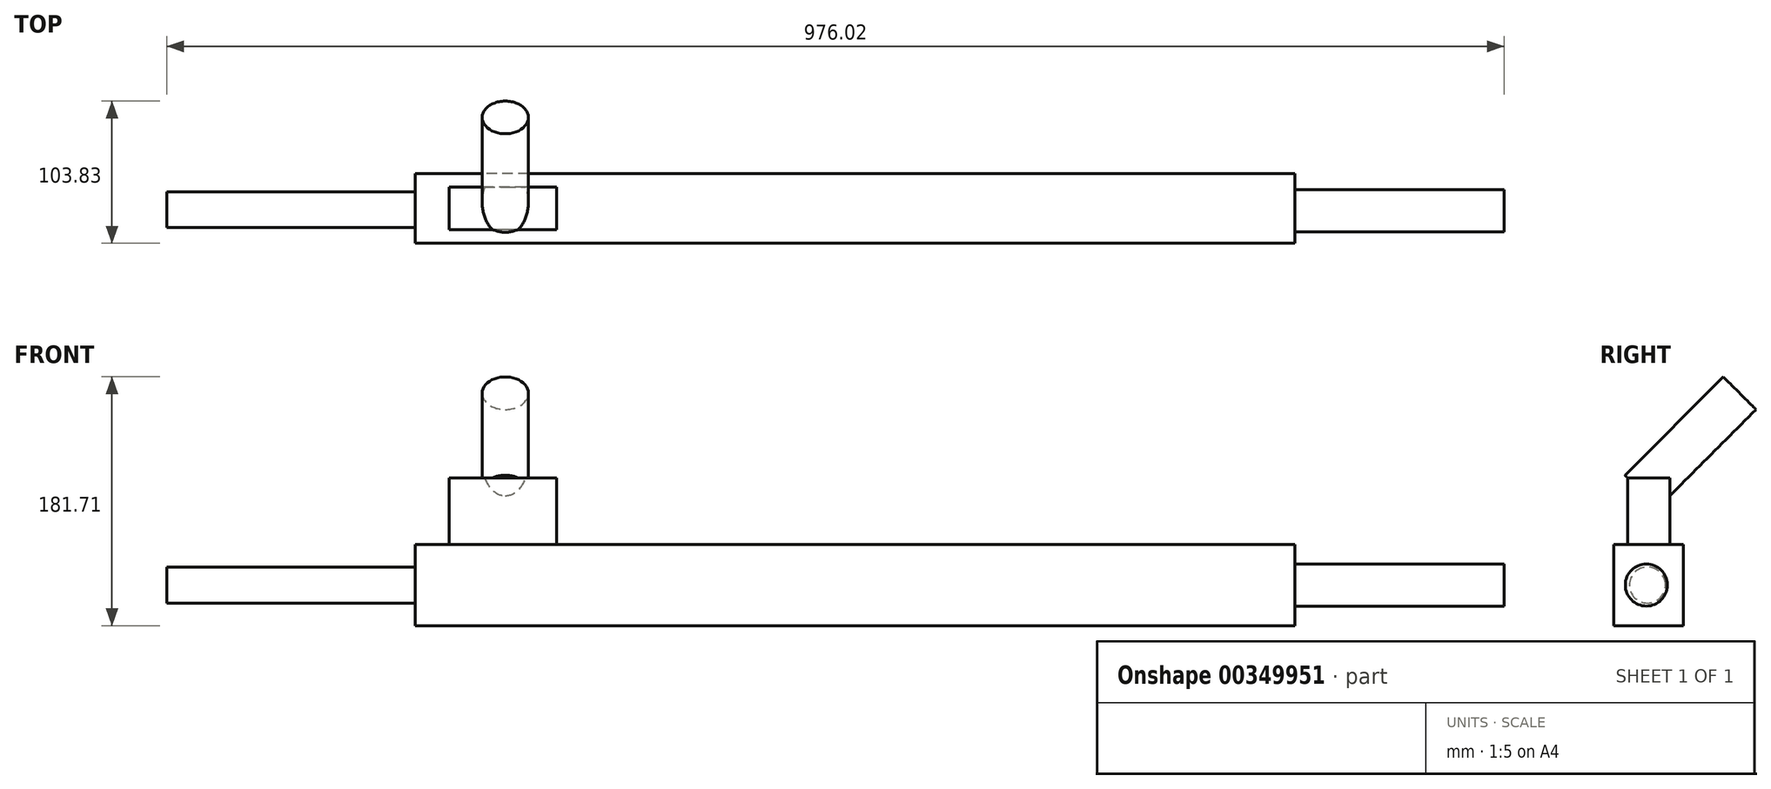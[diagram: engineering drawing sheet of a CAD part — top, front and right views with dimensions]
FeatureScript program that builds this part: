
annotation { "Feature Type Name" : "Feature", "Feature Type Description" : "" }
export const myFeature = defineFeature(function(context is Context, id is Id, definition is map)
    precondition{}
    {
        {
            var Q0;
            Q0=qCreatedBy(makeId("Front.planeOp"),FACE);
            var sketch = newSketch(context, id + "F0", { "sketchPlane" : qUnion([Q0])});
            skLineSegment(sketch, "E0.bottom", {"start": v(321, -29.68) * mm, "end": v(-321, -29.68) * mm});
            skLineSegment(sketch, "E0.top", {"start": v(321, 29.68) * mm, "end": v(-321, 29.68) * mm});
            skLineSegment(sketch, "E0.left", {"start": v(321, -29.68) * mm, "end": v(321, 29.68) * mm});
            skLineSegment(sketch, "E0.right", {"start": v(-321, -29.68) * mm, "end": v(-321, 29.68) * mm});
            skPoint(sketch, "E0.middle", {"position": v(0, 0) * mm});
            skSolve(sketch);
        }
        {
            var Q0;
            Q0 = qSketchRegion(id + "F0", true);
            extrude(context, id + "F1", {"entities" : qUnion([Q0]), "depth" : 50.8 * mm});
        }
        {
            var Q0;
            Q0=makeQuery(id+"F1.opExtrude","SWEPT_FACE",FACE,{"disambiguationData":[OSD([sQuery(id+"F0.wireOp",EDGE,"E0.right")])]});
            var sketch = newSketch(context, id + "F2", { "sketchPlane" : qUnion([Q0])});
            skCircle(sketch, "E1", {"center": v(26.23, 0) * mm, "radius": 13.14 * mm});
            skSolve(sketch);
        }
        {
            var Q0;
            Q0 = qSketchRegion(id + "F2", true);
            extrude(context, id + "F3", {"entities" : qUnion([Q0]), "operationType" : NewBodyOperationType.ADD, "depth" : 181.36 * mm});
        }
        {
            var Q0;
            Q0=makeQuery(id+"F1.opExtrude","SWEPT_FACE",FACE,{"disambiguationData":[OSD([sQuery(id+"F0.wireOp",EDGE,"E0.left")])]});
            var sketch = newSketch(context, id + "F4", { "sketchPlane" : qUnion([Q0])});
            skCircle(sketch, "E2", {"center": v(-27.02, 0) * mm, "radius": 15.36 * mm});
            skSolve(sketch);
        }
        {
            var Q0;
            Q0 = qSketchRegion(id + "F4", true);
            extrude(context, id + "F5", {"entities" : qUnion([Q0]), "operationType" : NewBodyOperationType.ADD, "depth" : 152.65 * mm});
        }
        {
            var Q0;
            Q0=makeQuery(id+"F1.opExtrude","SWEPT_FACE",FACE,{"disambiguationData":[OSD([sQuery(id+"F0.wireOp",EDGE,"E0.top")])]});
            var sketch = newSketch(context, id + "F6", { "sketchPlane" : qUnion([Q0])});
            skLineSegment(sketch, "E3.bottom", {"start": v(-217.76, -40.7) * mm, "end": v(-296.39, -40.7) * mm});
            skLineSegment(sketch, "E3.top", {"start": v(-217.76, -9.88) * mm, "end": v(-296.39, -9.88) * mm});
            skLineSegment(sketch, "E3.left", {"start": v(-217.76, -40.7) * mm, "end": v(-217.76, -9.88) * mm});
            skLineSegment(sketch, "E3.right", {"start": v(-296.39, -40.7) * mm, "end": v(-296.39, -9.88) * mm});
            skPoint(sketch, "E3.middle", {"position": v(-257.07, -25.28) * mm});
            skSolve(sketch);
        }
        {
            var Q0;
            Q0 = qSketchRegion(id + "F6", true);
            extrude(context, id + "F7", {"entities" : qUnion([Q0]), "operationType" : NewBodyOperationType.ADD, "depth" : 48.5 * mm});
        }
        {
            var Q0;
            Q0=makeQuery(id+"F7.opExtrude","CAP_EDGE",EDGE,{"disambiguationData":[OSD([sQuery(id+"F6.wireOp",EDGE,"E3.bottom")])],"isStart":false});
            var Q1;
            Q1=makeQuery(id+"F7.opExtrude","CAP_FACE",FACE,{"disambiguationData":[OSD([sQuery(id+"F6.wireOp",EDGE,"E3.bottom"),sQuery(id+"F6.wireOp",EDGE,"E3.top"),sQuery(id+"F6.wireOp",EDGE,"E3.left"),sQuery(id+"F6.wireOp",EDGE,"E3.right")])],"isStart":false});
            cPlane(context, id + "F8", {"entities" : qUnion([Q0, Q1]), "cplaneType" : CPlaneType.LINE_ANGLE, "offset" : 25.4 * mm, "angle" : 45 * degree, "width" : 152.4 * mm, "height" : 152.4 * mm});
        }
        {
            var Q0;
            Q0=qCreatedBy(id+"F8.planeOp",FACE);
            var sketch = newSketch(context, id + "F9", { "sketchPlane" : qUnion([Q0])});
            skCircle(sketch, "E4", {"center": v(-255.31, 70) * mm, "radius": 16.89 * mm});
            skSolve(sketch);
        }
        {
            var Q0;
            Q0 = qSketchRegion(id + "F9", true);
            extrude(context, id + "F10", {"entities" : qUnion([Q0]), "operationType" : NewBodyOperationType.ADD, "oppositeDirection" : true, "depth" : 101.6 * mm});
        }
    });
